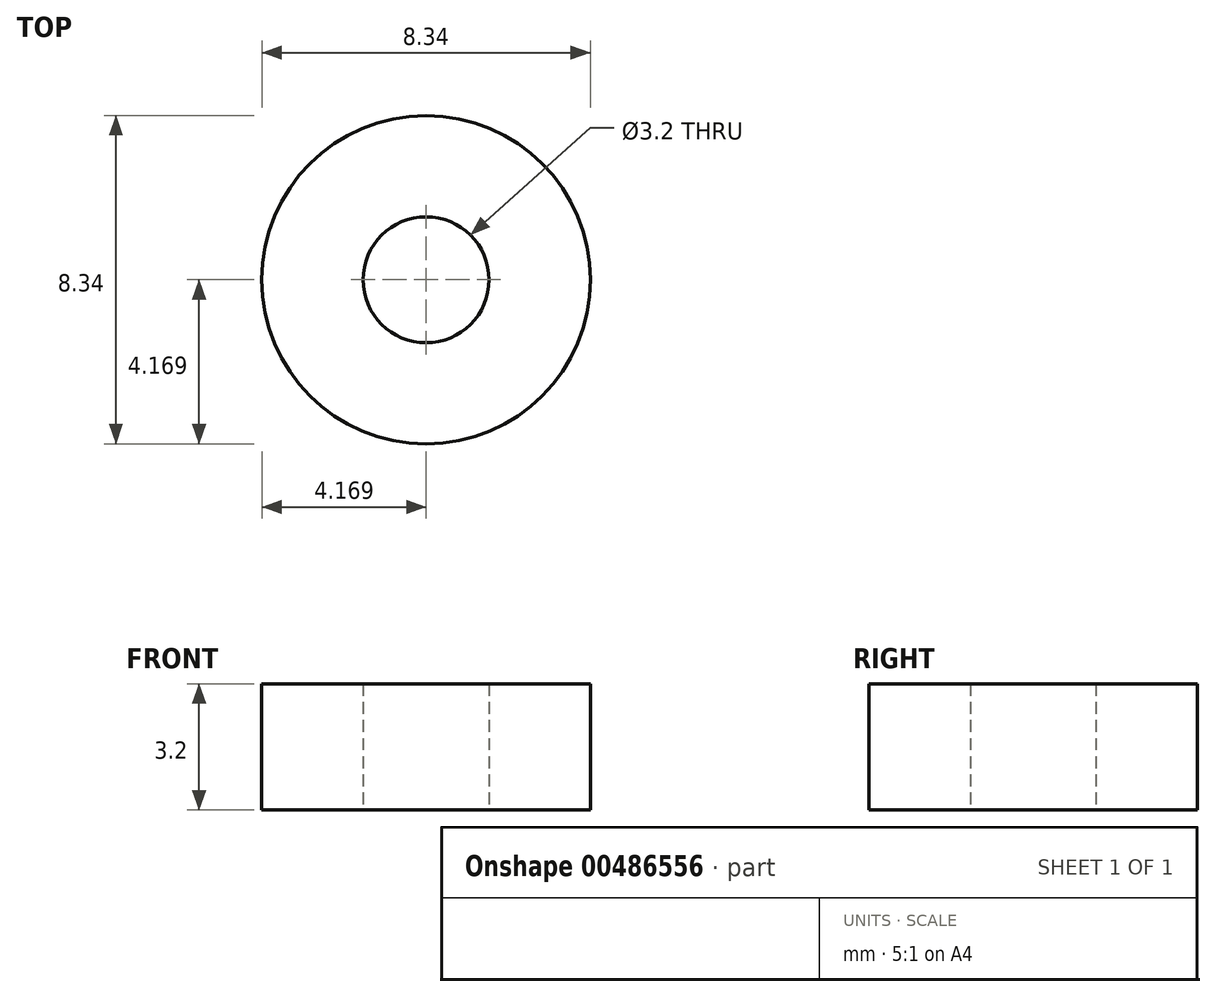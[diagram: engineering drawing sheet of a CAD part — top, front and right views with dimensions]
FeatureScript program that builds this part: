
annotation { "Feature Type Name" : "Feature", "Feature Type Description" : "" }
export const myFeature = defineFeature(function(context is Context, id is Id, definition is map)
    precondition{}
    {
        {
            var Q0;
            Q0=qCreatedBy(makeId("Top.planeOp"),FACE);
            var sketch = newSketch(context, id + "F0", { "sketchPlane" : qUnion([Q0])});
            skCircle(sketch, "E0", {"center": v(-37.95, 33.32) * mm, "radius": 4.17 * mm});
            skCircle(sketch, "E1", {"center": v(-37.95, 33.32) * mm, "radius": 1.6 * mm});
            skSolve(sketch);
        }
        {
            var Q0;
            Q0=makeQuery(id+"F0.imprint","IMPRINT",FACE,{"disambiguationData":[TD([[makeQuery(id+"F0.imprint","IMPRINT",EDGE,{"derivedFrom":sQuery(id+"F0.wireOp",EDGE,"E0")}),1.0]])]});
            extrude(context, id + "F1", {"entities" : qUnion([Q0]), "depth" : 3.2 * mm, "offsetDistance" : 25 * mm});
        }
    });
